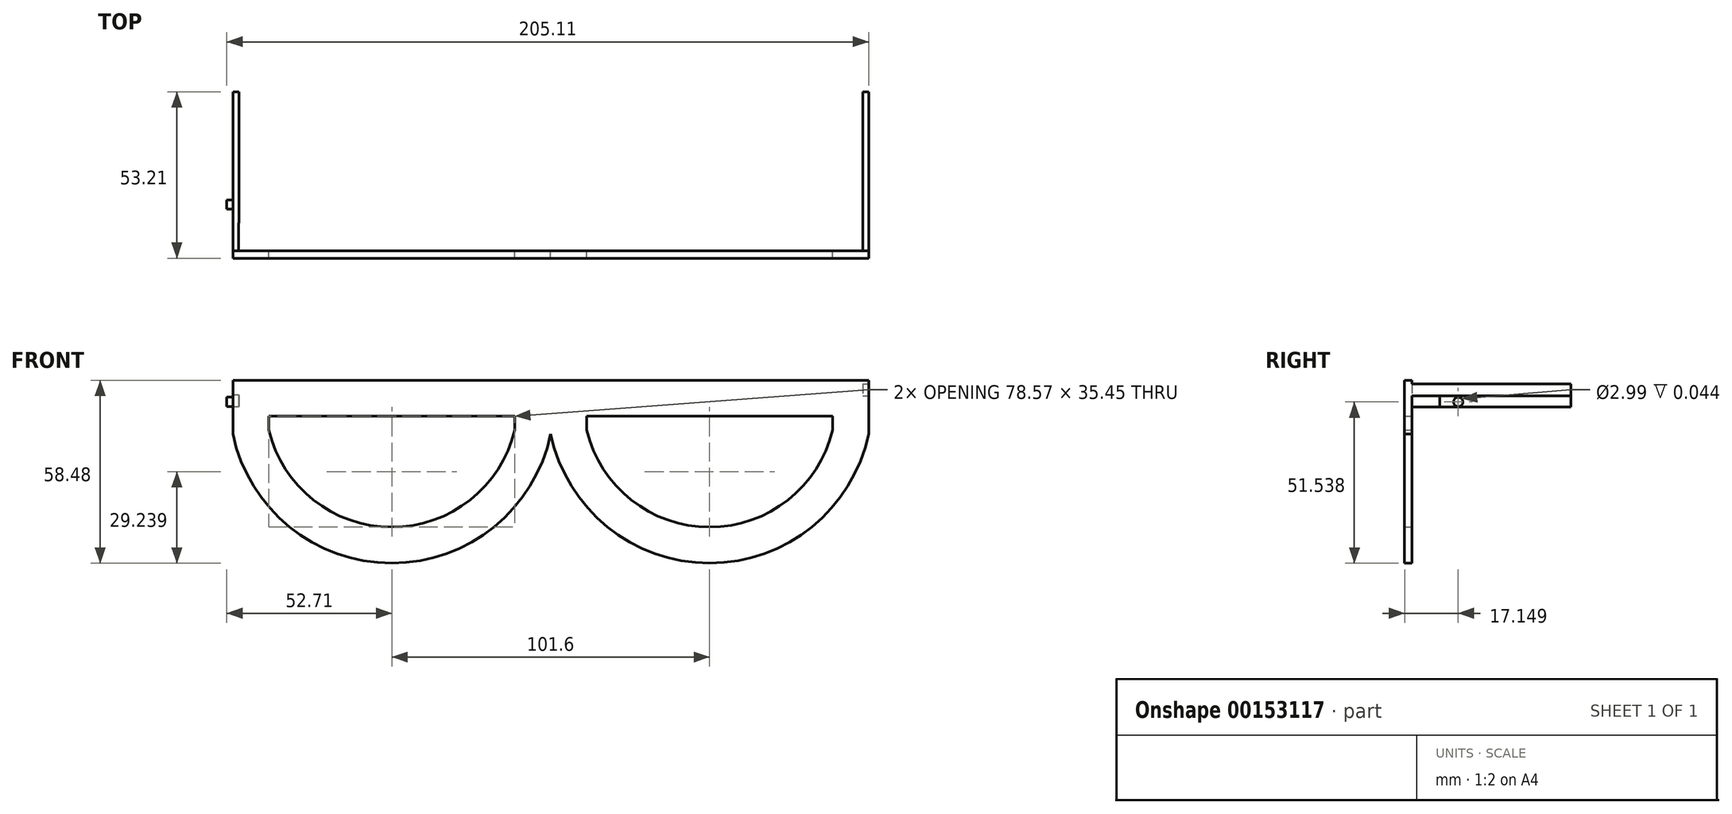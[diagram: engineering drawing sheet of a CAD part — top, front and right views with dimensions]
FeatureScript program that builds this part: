
annotation { "Feature Type Name" : "Feature", "Feature Type Description" : "" }
export const myFeature = defineFeature(function(context is Context, id is Id, definition is map)
    precondition{}
    {
        {
            var Q0;
            Q0=qCreatedBy(makeId("Front.planeOp"),FACE);
            var sketch = newSketch(context, id + "F0", { "sketchPlane" : qUnion([Q0])});
            skLineSegment(sketch, "E0", {"start": v(101.6, 0) * mm, "end": v(0, 0) * mm});
            skLineSegment(sketch, "E1", {"start": v(0, 0) * mm, "end": v(-101.6, 0) * mm});
            skLineSegment(sketch, "E2", {"start": v(101.6, 0) * mm, "end": v(101.6, -17.23) * mm});
            skLineSegment(sketch, "E3", {"start": v(0, -11.52) * mm, "end": v(0, -17.23) * mm});
            skArc(sketch, "E4", {"start": v(0, -17.23) * mm, "mid": v(50.8, -58.48) * mm, "end": v(101.6, -17.23) * mm});
            skLineSegment(sketch, "E5.MirrorCS", {"start": v(-101.6, 0) * mm, "end": v(-101.6, -17.23) * mm});
            skLineSegment(sketch, "E6.MirrorCS", {"start": v(-101.6, 0) * mm, "end": v(0, 0) * mm});
            skArc(sketch, "E7.MirrorCS", {"start": v(0, -17.23) * mm, "mid": v(-50.8, -58.48) * mm, "end": v(-101.6, -17.23) * mm});
            skLineSegment(sketch, "E8.0", {"start": v(90.08, -11.52) * mm, "end": v(11.52, -11.52) * mm});
            skLineSegment(sketch, "E9.0", {"start": v(90.08, -11.52) * mm, "end": v(90.08, -17.23) * mm});
            skArc(sketch, "E10.0", {"start": v(11.27, -14.87) * mm, "mid": v(50.8, -46.96) * mm, "end": v(90.33, -14.87) * mm});
            skArc(sketch, "E11.0", {"start": v(-11.27, -14.87) * mm, "mid": v(-50.8, -46.96) * mm, "end": v(-90.33, -14.87) * mm});
            skLineSegment(sketch, "E12.0", {"start": v(-90.08, -11.52) * mm, "end": v(-90.08, -17.23) * mm});
            skLineSegment(sketch, "E13.0", {"start": v(-11.52, -11.52) * mm, "end": v(-11.52, -17.23) * mm});
            skLineSegment(sketch, "E14.0", {"start": v(-90.08, -11.52) * mm, "end": v(-11.52, -11.52) * mm});
            skLineSegment(sketch, "E15.0", {"start": v(11.52, -11.52) * mm, "end": v(11.52, -17.23) * mm});
            skSolve(sketch);
        }
        {
            var Q0;
            Q0=makeQuery(id+"F0.imprint","IMPRINT",FACE,{"disambiguationData":[TD([[makeQuery(id+"F0.imprint","IMPRINT",EDGE,{"derivedFrom":sQuery(id+"F0.wireOp",EDGE,"E0")}),1.0]])]});
            extrude(context, id + "F1", {"entities" : qUnion([Q0]), "depth" : 2.41 * mm});
        }
        {
            var Q0;
            Q0=makeQuery(id+"F1.opExtrude","SWEPT_FACE",FACE,{"disambiguationData":[OSD([sQuery(id+"F0.wireOp",EDGE,"E5.MirrorCS")])]});
            var sketch = newSketch(context, id + "F2", { "sketchPlane" : qUnion([Q0])});
            skLineSegment(sketch, "E16", {"start": v(0, -4.8) * mm, "end": v(-50.8, -4.8) * mm});
            skLineSegment(sketch, "E17", {"start": v(-50.8, -4.8) * mm, "end": v(-50.8, -8.61) * mm});
            skPoint(sketch, "E17.endSnap0", {"position": v(2.41, -8.61) * mm});
            skLineSegment(sketch, "E18", {"start": v(-50.8, -8.61) * mm, "end": v(0, -8.61) * mm});
            skLineSegment(sketch, "E19", {"start": v(0, -8.61) * mm, "end": v(-0.36, -5.42) * mm});
            skSolve(sketch);
        }
        {
            var Q0;
            Q0=makeQuery(id+"F1.opExtrude","SWEPT_FACE",FACE,{"disambiguationData":[OSD([sQuery(id+"F0.wireOp",EDGE,"E2")])]});
            var sketch = newSketch(context, id + "F3", { "sketchPlane" : qUnion([Q0])});
            skLineSegment(sketch, "E20", {"start": v(0, -1.18) * mm, "end": v(50.8, -1.18) * mm});
            skLineSegment(sketch, "E21", {"start": v(50.8, -1.18) * mm, "end": v(50.8, -5) * mm});
            skLineSegment(sketch, "E22", {"start": v(50.8, -5) * mm, "end": v(0, -5) * mm});
            skSolve(sketch);
        }
        {
            var Q0;
            {var subQ0=sQuery(id+"F3.wireOp",EDGE,"E20");Q0=makeQuery(id+"F3.imprint","IMPRINT",FACE,{"disambiguationData":[TD([[makeQuery(id+"F3.imprint","IMPRINT",EDGE,{"derivedFrom":subQ0}),-1.0]])]});}
            extrude(context, id + "F4", {"entities" : qUnion([Q0]), "operationType" : NewBodyOperationType.ADD, "oppositeDirection" : true, "depth" : 1.9 * mm});
        }
        {
            var Q0;
            {var subQ0=sQuery(id+"F2.wireOp",EDGE,"E17");Q0=makeQuery(id+"F2.imprint","IMPRINT",FACE,{"disambiguationData":[TD([[makeQuery(id+"F2.imprint","IMPRINT",EDGE,{"derivedFrom":subQ0}),1.0]])]});}
            extrude(context, id + "F5", {"entities" : qUnion([Q0]), "oppositeDirection" : true, "depth" : 1.9 * mm});
        }
        {
            var Q0;
            Q0=makeQuery(id+"F5.opExtrude","CAP_FACE",FACE,{"disambiguationData":[OSD([sQuery(id+"F2.wireOp",EDGE,"E16"),sQuery(id+"F2.wireOp",EDGE,"E17"),sQuery(id+"F2.wireOp",EDGE,"E18"),sQuery(id+"F2.wireOp",EDGE,"E19")])],"isStart":true});
            var sketch = newSketch(context, id + "F6", { "sketchPlane" : qUnion([Q0])});
            skLineSegment(sketch, "E23", {"start": v(-8.82, -4.8) * mm, "end": v(-8.82, -8.61) * mm});
            skLineSegment(sketch, "E24", {"start": v(-10.56, -3.16) * mm, "end": v(-7.21, -3.16) * mm});
            skLineSegment(sketch, "E25", {"start": v(-4.78, -3.4) * mm, "end": v(-1.75, -3.4) * mm});
            skSolve(sketch);
        }
        {
            var Q0;
            {var subQ0=sQuery(id+"F6.wireOp",EDGE,"E23");Q0=makeQuery(id+"F6.imprint","IMPRINT",FACE,{"disambiguationData":[TD([[makeQuery(id+"F6.imprint","IMPRINT",EDGE,{"derivedFrom":subQ0}),-1.0]])]});}
            var sketch = newSketch(context, id + "F7", { "sketchPlane" : qUnion([Q0])});
            skCircle(sketch, "E26", {"center": v(-14.74, -6.94) * mm, "radius": 1.5 * mm});
            skSolve(sketch);
        }
        {
            var Q0;
            {var subQ2=sQuery(id+"F6.wireOp",EDGE,"E23");var subQ4=makeQuery(id+"F6.imprint","IMPRINT",EDGE,{"derivedFrom":subQ2});Q0=makeQuery(id+"F7.imprint","IMPRINT",FACE,{"disambiguationData":[TD([[makeQuery(id+"F7.imprint","IMPRINT",EDGE,{"derivedFrom":subQ4}),-1.0]])]});}
            extrude(context, id + "F8", {"entities" : qUnion([Q0]), "operationType" : NewBodyOperationType.ADD, "oppositeDirection" : true, "depth" : 1.95 * mm});
        }
        {
            var Q0;
            Q0=makeQuery(id+"F7.imprint","IMPRINT",FACE,{"disambiguationData":[TD([[makeQuery(id+"F7.imprint","IMPRINT",EDGE,{"derivedFrom":sQuery(id+"F7.wireOp",EDGE,"E26")}),1.0]])]});
            extrude(context, id + "F9", {"entities" : qUnion([Q0]), "operationType" : NewBodyOperationType.ADD, "depth" : 1.9 * mm});
        }
    });
